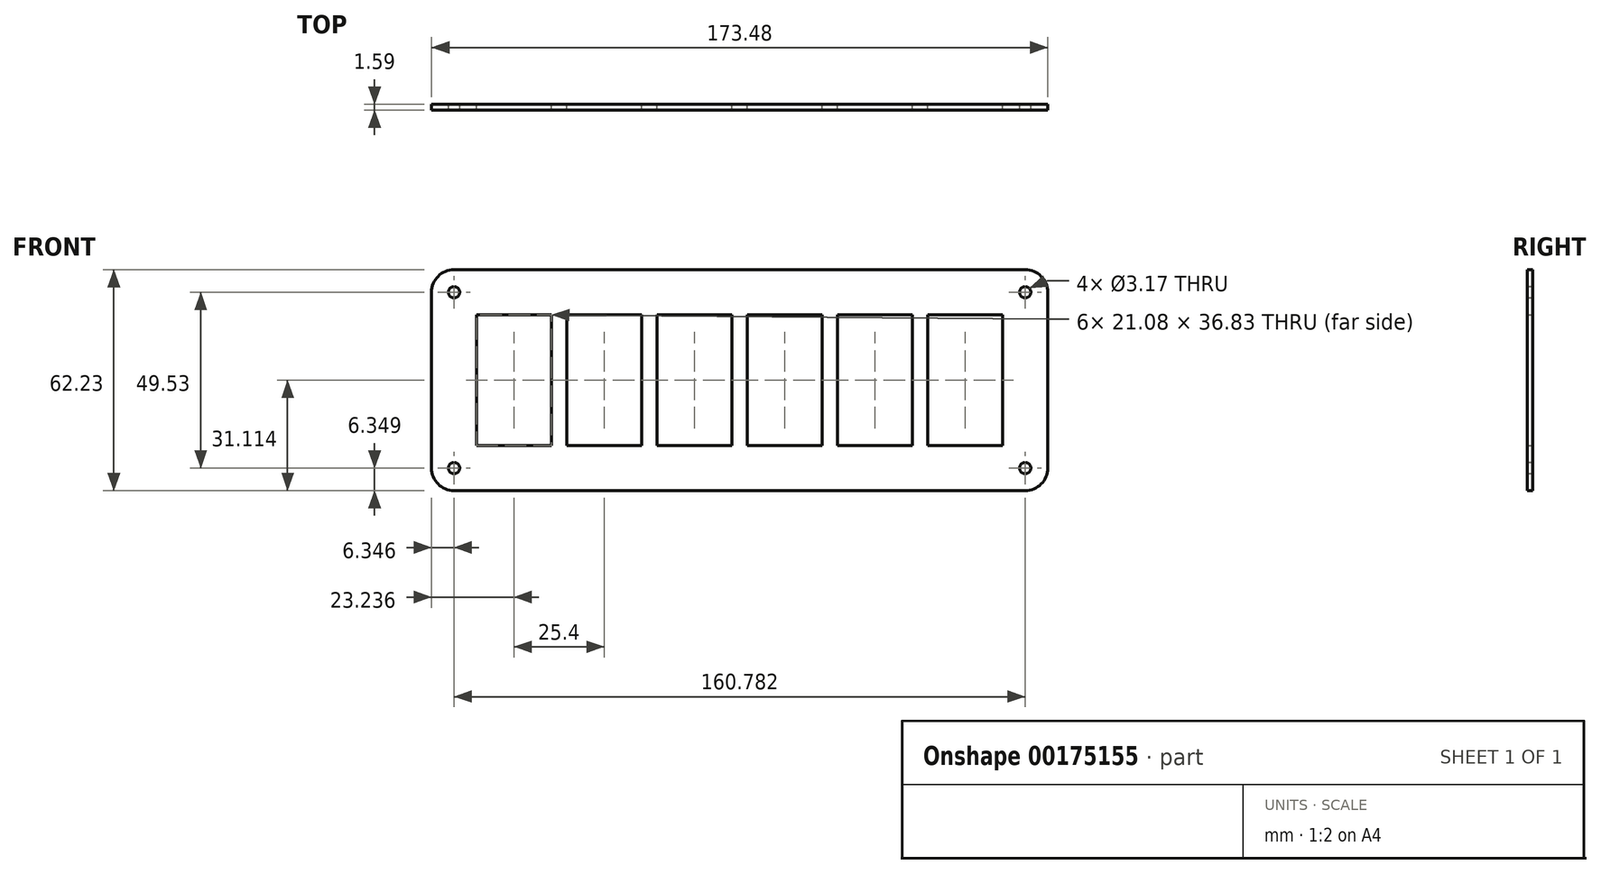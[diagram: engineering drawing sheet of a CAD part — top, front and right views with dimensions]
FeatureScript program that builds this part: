
annotation { "Feature Type Name" : "Feature", "Feature Type Description" : "" }
export const myFeature = defineFeature(function(context is Context, id is Id, definition is map)
    precondition{}
    {
        {
            var Q0;
            Q0=qCreatedBy(makeId("Front.planeOp"),FACE);
            var sketch = newSketch(context, id + "F0", { "sketchPlane" : qUnion([Q0])});
            skLineSegment(sketch, "E0.bottom", {"start": v(-68.3, 59.79) * mm, "end": v(92.49, 59.79) * mm});
            skLineSegment(sketch, "E0.top", {"start": v(-68.3, -2.44) * mm, "end": v(92.49, -2.44) * mm});
            skLineSegment(sketch, "E0.left", {"start": v(-74.64, 53.44) * mm, "end": v(-74.64, 3.9) * mm});
            skLineSegment(sketch, "E0.right", {"start": v(98.84, 53.44) * mm, "end": v(98.84, 3.9) * mm});
            skLineSegment(sketch, "E1", {"start": v(-61.94, 47.09) * mm, "end": v(-61.94, 10.26) * mm});
            skLineSegment(sketch, "E2", {"start": v(-40.86, 47.09) * mm, "end": v(-40.86, 10.26) * mm});
            skLineSegment(sketch, "E3", {"start": v(-61.94, 47.09) * mm, "end": v(-40.86, 47.09) * mm});
            skPoint(sketch, "E4.orphan", {"position": v(-74.64, 28.67) * mm});
            skLineSegment(sketch, "E5.trimOffspring", {"start": v(-40.86, 10.26) * mm, "end": v(-61.94, 10.26) * mm});
            skLineSegment(sketch, "E6.1.0.0", {"start": v(-36.54, 47.09) * mm, "end": v(-15.46, 47.09) * mm});
            skLineSegment(sketch, "E6.1.0.1", {"start": v(-36.54, 47.09) * mm, "end": v(-36.54, 10.26) * mm});
            skLineSegment(sketch, "E6.1.0.2", {"start": v(-15.46, 47.09) * mm, "end": v(-15.46, 10.26) * mm});
            skLineSegment(sketch, "E6.1.0.3", {"start": v(-15.46, 10.26) * mm, "end": v(-36.54, 10.26) * mm});
            skLineSegment(sketch, "E6.2.0.0", {"start": v(-11.14, 47.09) * mm, "end": v(9.94, 47.09) * mm});
            skLineSegment(sketch, "E6.2.0.1", {"start": v(-11.14, 47.09) * mm, "end": v(-11.14, 10.26) * mm});
            skLineSegment(sketch, "E6.2.0.2", {"start": v(9.94, 47.09) * mm, "end": v(9.94, 10.26) * mm});
            skLineSegment(sketch, "E6.2.0.3", {"start": v(9.94, 10.26) * mm, "end": v(-11.14, 10.26) * mm});
            skLineSegment(sketch, "E6.3.0.0", {"start": v(14.26, 47.09) * mm, "end": v(35.34, 47.09) * mm});
            skLineSegment(sketch, "E6.3.0.1", {"start": v(14.26, 47.09) * mm, "end": v(14.26, 10.26) * mm});
            skLineSegment(sketch, "E6.3.0.2", {"start": v(35.34, 47.09) * mm, "end": v(35.34, 10.26) * mm});
            skLineSegment(sketch, "E6.3.0.3", {"start": v(35.34, 10.26) * mm, "end": v(14.26, 10.26) * mm});
            skLineSegment(sketch, "E6.4.0.0", {"start": v(39.66, 47.09) * mm, "end": v(60.74, 47.09) * mm});
            skLineSegment(sketch, "E6.4.0.1", {"start": v(39.66, 47.09) * mm, "end": v(39.66, 10.26) * mm});
            skLineSegment(sketch, "E6.4.0.2", {"start": v(60.74, 47.09) * mm, "end": v(60.74, 10.26) * mm});
            skLineSegment(sketch, "E6.4.0.3", {"start": v(60.74, 10.26) * mm, "end": v(39.66, 10.26) * mm});
            skLineSegment(sketch, "E6.5.0.0", {"start": v(65.06, 47.09) * mm, "end": v(86.14, 47.09) * mm});
            skLineSegment(sketch, "E6.5.0.1", {"start": v(65.06, 47.09) * mm, "end": v(65.06, 10.26) * mm});
            skLineSegment(sketch, "E6.5.0.2", {"start": v(86.14, 47.09) * mm, "end": v(86.14, 10.26) * mm});
            skLineSegment(sketch, "E6.5.0.3", {"start": v(86.14, 10.26) * mm, "end": v(65.06, 10.26) * mm});
            skLineSegment(sketch, "E6.direction1", {"start": v(-61.94, 47.09) * mm, "end": v(-36.54, 47.09) * mm, "construction": true});
            skPoint(sketch, "E7.visualSharp", {"position": v(-74.64, 59.79) * mm});
            skArc(sketch, "E7.filletArc", {"start": v(-68.3, 59.79) * mm, "mid": v(-72.78, 57.93) * mm, "end": v(-74.64, 53.44) * mm});
            skPoint(sketch, "E8.visualSharp", {"position": v(98.84, 59.79) * mm});
            skArc(sketch, "E8.filletArc", {"start": v(98.84, 53.44) * mm, "mid": v(96.98, 57.93) * mm, "end": v(92.49, 59.79) * mm});
            skPoint(sketch, "E9.visualSharp", {"position": v(98.84, -2.44) * mm});
            skArc(sketch, "E9.filletArc", {"start": v(92.49, -2.44) * mm, "mid": v(96.98, -0.58) * mm, "end": v(98.84, 3.9) * mm});
            skPoint(sketch, "E10.visualSharp", {"position": v(-74.64, -2.44) * mm});
            skArc(sketch, "E10.filletArc", {"start": v(-74.64, 3.9) * mm, "mid": v(-72.78, -0.58) * mm, "end": v(-68.3, -2.44) * mm});
            skCircle(sketch, "E11", {"center": v(-68.3, 3.9) * mm, "radius": 1.59 * mm});
            skCircle(sketch, "E12", {"center": v(-68.3, 53.44) * mm, "radius": 1.59 * mm});
            skCircle(sketch, "E13", {"center": v(92.49, 53.44) * mm, "radius": 1.59 * mm});
            skCircle(sketch, "E14", {"center": v(92.49, 3.9) * mm, "radius": 1.59 * mm});
            skSolve(sketch);
        }
        {
            var Q0;
            Q0 = qSketchRegion(id + "F0", true);
            extrude(context, id + "F1", {"entities" : qUnion([Q0]), "depth" : 1.59 * mm});
        }
    });
